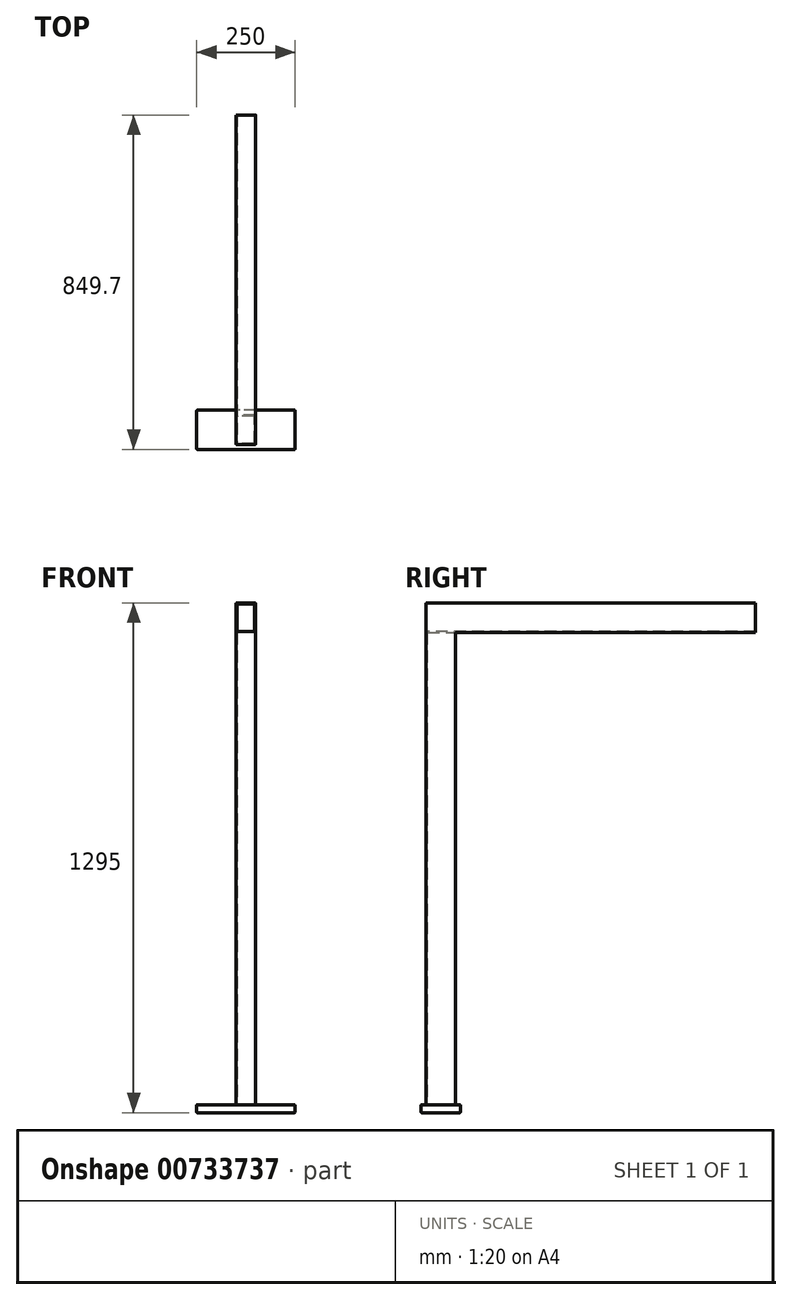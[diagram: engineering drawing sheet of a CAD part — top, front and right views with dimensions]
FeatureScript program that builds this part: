
annotation { "Feature Type Name" : "Feature", "Feature Type Description" : "" }
export const myFeature = defineFeature(function(context is Context, id is Id, definition is map)
    precondition{}
    {
        {
            var Q0;
            Q0=qCreatedBy(makeId("Top.planeOp"),FACE);
            var sketch = newSketch(context, id + "F0", { "sketchPlane" : qUnion([Q0])});
            skLineSegment(sketch, "E0.bottom", {"start": v(125, -50) * mm, "end": v(-125, -50) * mm});
            skLineSegment(sketch, "E0.top", {"start": v(125, 50) * mm, "end": v(-125, 50) * mm});
            skLineSegment(sketch, "E0.left", {"start": v(125, -50) * mm, "end": v(125, 50) * mm});
            skLineSegment(sketch, "E0.right", {"start": v(-125, -50) * mm, "end": v(-125, 50) * mm});
            skPoint(sketch, "E0.middle", {"position": v(0, 0) * mm});
            skSolve(sketch);
        }
        {
            var Q0;
            Q0=makeQuery(id+"F0.imprint","IMPRINT",FACE,{"disambiguationData":[TD([[makeQuery(id+"F0.imprint","IMPRINT",EDGE,{"derivedFrom":sQuery(id+"F0.wireOp",EDGE,"E0.bottom")}),-1.0]])]});
            extrude(context, id + "F1", {"entities" : qUnion([Q0]), "depth" : 20 * mm, "offsetDistance" : 25 * mm});
        }
        {
            var Q0;
            Q0=makeQuery(id+"F1.opExtrude","CAP_FACE",FACE,{"disambiguationData":[OSD([sQuery(id+"F0.wireOp",EDGE,"E0.bottom"),sQuery(id+"F0.wireOp",EDGE,"E0.top"),sQuery(id+"F0.wireOp",EDGE,"E0.left"),sQuery(id+"F0.wireOp",EDGE,"E0.right")])],"isStart":false});
            var sketch = newSketch(context, id + "F2", { "sketchPlane" : qUnion([Q0])});
            skLineSegment(sketch, "E1.bottom", {"start": v(25, -37.5) * mm, "end": v(-25, -37.5) * mm});
            skLineSegment(sketch, "E1.top", {"start": v(25, 37.5) * mm, "end": v(-25, 37.5) * mm});
            skLineSegment(sketch, "E1.left", {"start": v(25, -37.5) * mm, "end": v(25, 37.5) * mm});
            skLineSegment(sketch, "E1.right", {"start": v(-25, -37.5) * mm, "end": v(-25, 37.5) * mm});
            skPoint(sketch, "E1.middle", {"position": v(0, 0) * mm});
            skLineSegment(sketch, "E2.0", {"start": v(22, -34.5) * mm, "end": v(22, 34.5) * mm});
            skLineSegment(sketch, "E2.1", {"start": v(22, -34.5) * mm, "end": v(-22, -34.5) * mm});
            skLineSegment(sketch, "E2.2", {"start": v(-22, -34.5) * mm, "end": v(-22, 34.5) * mm});
            skLineSegment(sketch, "E2.3", {"start": v(22, 34.5) * mm, "end": v(-22, 34.5) * mm});
            skSolve(sketch);
        }
        {
            var Q0;
            Q0=makeQuery(id+"F2.imprint","IMPRINT",FACE,{"disambiguationData":[TD([[makeQuery(id+"F2.imprint","IMPRINT",EDGE,{"derivedFrom":sQuery(id+"F2.wireOp",EDGE,"E1.bottom")}),-1.0]])]});
            extrude(context, id + "F3", {"entities" : qUnion([Q0]), "operationType" : NewBodyOperationType.ADD, "depth" : 1200 * mm, "offsetDistance" : 25 * mm});
        }
        {
            var Q0;
            Q0=makeQuery(id+"F3.opExtrude","SWEPT_FACE",FACE,{"disambiguationData":[OSD([sQuery(id+"F2.wireOp",EDGE,"E1.bottom")])]});
            var sketch = newSketch(context, id + "F4", { "sketchPlane" : qUnion([Q0])});
            skLineSegment(sketch, "E3.bottom", {"start": v(25, 1220) * mm, "end": v(-25, 1220) * mm});
            skLineSegment(sketch, "E3.top", {"start": v(25, 1295) * mm, "end": v(-25, 1295) * mm});
            skLineSegment(sketch, "E3.left", {"start": v(25, 1220) * mm, "end": v(25, 1295) * mm});
            skLineSegment(sketch, "E3.right", {"start": v(-25, 1220) * mm, "end": v(-25, 1295) * mm});
            skLineSegment(sketch, "E4.0", {"start": v(-22, 1223) * mm, "end": v(-22, 1292) * mm});
            skLineSegment(sketch, "E4.1", {"start": v(22, 1223) * mm, "end": v(-22, 1223) * mm});
            skLineSegment(sketch, "E4.2", {"start": v(22, 1223) * mm, "end": v(22, 1292) * mm});
            skLineSegment(sketch, "E4.3", {"start": v(22, 1292) * mm, "end": v(-22, 1292) * mm});
            skSolve(sketch);
        }
        {
            var Q0;
            Q0=makeQuery(id+"F4.imprint","IMPRINT",FACE,{"disambiguationData":[TD([[makeQuery(id+"F4.imprint","IMPRINT",EDGE,{"derivedFrom":sQuery(id+"F4.wireOp",EDGE,"E3.bottom")}),-1.0]])]});
            extrude(context, id + "F5", {"entities" : qUnion([Q0]), "operationType" : NewBodyOperationType.ADD, "oppositeDirection" : true, "depth" : 837.2 * mm, "offsetDistance" : 25 * mm});
        }
        {
            var Q0;
            Q0=makeQuery(id+"F5.boolean.opBoolean","MERGE",EDGE,{"derivedFrom":[makeQuery(id+"F3.opExtrude","SWEPT_EDGE",EDGE,{"disambiguationData":[OSD([sQuery(id+"F2.wireOp",EDGE,"E1.bottom"),sQuery(id+"F2.wireOp",EDGE,"E1.right")])]}),makeQuery(id+"F5.opExtrude","CAP_EDGE",EDGE,{"disambiguationData":[OSD([sQuery(id+"F4.wireOp",EDGE,"E3.right")])],"isStart":true})]});
            var Q1;
            Q1=makeQuery(id+"F3.opExtrude","SWEPT_EDGE",EDGE,{"disambiguationData":[OSD([sQuery(id+"F2.wireOp",EDGE,"E1.top"),sQuery(id+"F2.wireOp",EDGE,"E1.left")])]});
            var Q2;
            Q2=makeQuery(id+"F5.boolean.opBoolean","MERGE",EDGE,{"derivedFrom":[makeQuery(id+"F3.opExtrude","SWEPT_EDGE",EDGE,{"disambiguationData":[OSD([sQuery(id+"F2.wireOp",EDGE,"E1.bottom"),sQuery(id+"F2.wireOp",EDGE,"E1.left")])]}),makeQuery(id+"F5.opExtrude","CAP_EDGE",EDGE,{"disambiguationData":[OSD([sQuery(id+"F4.wireOp",EDGE,"E3.left")])],"isStart":true})]});
            var Q3;
            Q3=makeQuery(id+"F3.opExtrude","SWEPT_EDGE",EDGE,{"disambiguationData":[OSD([sQuery(id+"F2.wireOp",EDGE,"E2.1"),sQuery(id+"F2.wireOp",EDGE,"E2.2")])]});
            var Q4;
            Q4=makeQuery(id+"F3.opExtrude","SWEPT_EDGE",EDGE,{"disambiguationData":[OSD([sQuery(id+"F2.wireOp",EDGE,"E2.0"),sQuery(id+"F2.wireOp",EDGE,"E2.3")])]});
            var Q5;
            Q5=makeQuery(id+"F3.opExtrude","SWEPT_EDGE",EDGE,{"disambiguationData":[OSD([sQuery(id+"F2.wireOp",EDGE,"E2.0"),sQuery(id+"F2.wireOp",EDGE,"E2.1")])]});
            var Q6;
            Q6=makeQuery(id+"F3.opExtrude","SWEPT_EDGE",EDGE,{"disambiguationData":[OSD([sQuery(id+"F2.wireOp",EDGE,"E2.2"),sQuery(id+"F2.wireOp",EDGE,"E2.3")])]});
            var Q7;
            Q7=makeQuery(id+"F3.opExtrude","SWEPT_EDGE",EDGE,{"disambiguationData":[OSD([sQuery(id+"F2.wireOp",EDGE,"E1.top"),sQuery(id+"F2.wireOp",EDGE,"E1.right")])]});
            var Q8;
            Q8=makeQuery(id+"F5.opExtrude","SWEPT_EDGE",EDGE,{"disambiguationData":[OSD([sQuery(id+"F4.wireOp",EDGE,"E3.top"),sQuery(id+"F4.wireOp",EDGE,"E3.left")])]});
            var Q9;
            Q9=makeQuery(id+"F5.opExtrude","SWEPT_EDGE",EDGE,{"disambiguationData":[OSD([sQuery(id+"F2.wireOp",EDGE,"E1.bottom"),sQuery(id+"F2.wireOp",EDGE,"E1.left"),sQuery(id+"F4.wireOp",EDGE,"E3.bottom"),sQuery(id+"F4.wireOp",EDGE,"E3.left")])]});
            var Q10;
            Q10=makeQuery(id+"F5.opExtrude","SWEPT_EDGE",EDGE,{"disambiguationData":[OSD([sQuery(id+"F4.wireOp",EDGE,"E3.top"),sQuery(id+"F4.wireOp",EDGE,"E3.right")])]});
            var Q11;
            Q11=makeQuery(id+"F5.opExtrude","SWEPT_EDGE",EDGE,{"disambiguationData":[OSD([sQuery(id+"F4.wireOp",EDGE,"E4.0"),sQuery(id+"F4.wireOp",EDGE,"E4.3")])]});
            var Q12;
            Q12=makeQuery(id+"F5.opExtrude","CAP_EDGE",EDGE,{"disambiguationData":[OSD([sQuery(id+"F4.wireOp",EDGE,"E4.0")])],"isStart":true});
            var Q13;
            Q13=makeQuery(id+"F5.opExtrude","CAP_EDGE",EDGE,{"disambiguationData":[OSD([sQuery(id+"F4.wireOp",EDGE,"E4.1")])],"isStart":true});
            var Q14;
            Q14=makeQuery(id+"F5.opExtrude","SWEPT_EDGE",EDGE,{"disambiguationData":[OSD([sQuery(id+"F4.wireOp",EDGE,"E4.2"),sQuery(id+"F4.wireOp",EDGE,"E4.3")])]});
            var Q15;
            Q15=makeQuery(id+"F3.opExtrude","CAP_EDGE",EDGE,{"disambiguationData":[OSD([sQuery(id+"F2.wireOp",EDGE,"E1.top")])],"isStart":false});
            var Q16;
            Q16=makeQuery(id+"F5.opExtrude","CAP_EDGE",EDGE,{"disambiguationData":[OSD([sQuery(id+"F4.wireOp",EDGE,"E3.top")])],"isStart":true});
            var Q17;
            Q17=makeQuery(id+"F5.opExtrude","SWEPT_EDGE",EDGE,{"disambiguationData":[OSD([sQuery(id+"F4.wireOp",EDGE,"E4.1"),sQuery(id+"F4.wireOp",EDGE,"E4.2")])]});
            var Q18;
            Q18=makeQuery(id+"F5.opExtrude","SWEPT_EDGE",EDGE,{"disambiguationData":[OSD([sQuery(id+"F4.wireOp",EDGE,"E4.0"),sQuery(id+"F4.wireOp",EDGE,"E4.1")])]});
            var Q19;
            Q19=makeQuery(id+"F3.opExtrude","CAP_EDGE",EDGE,{"disambiguationData":[OSD([sQuery(id+"F2.wireOp",EDGE,"E2.0")])],"isStart":false});
            var Q20;
            Q20=makeQuery(id+"F3.opExtrude","CAP_EDGE",EDGE,{"disambiguationData":[OSD([sQuery(id+"F2.wireOp",EDGE,"E2.1")])],"isStart":false});
            var Q21;
            Q21=makeQuery(id+"F3.opExtrude","CAP_EDGE",EDGE,{"disambiguationData":[OSD([sQuery(id+"F2.wireOp",EDGE,"E2.2")])],"isStart":false});
            var Q22;
            Q22=makeQuery(id+"F5.opExtrude","SWEPT_EDGE",EDGE,{"disambiguationData":[OSD([sQuery(id+"F2.wireOp",EDGE,"E1.bottom"),sQuery(id+"F2.wireOp",EDGE,"E1.right"),sQuery(id+"F4.wireOp",EDGE,"E3.bottom"),sQuery(id+"F4.wireOp",EDGE,"E3.right")])]});
            var Q23;
            Q23=makeQuery(id+"F3.opExtrude","CAP_EDGE",EDGE,{"disambiguationData":[OSD([sQuery(id+"F2.wireOp",EDGE,"E2.3")])],"isStart":false});
            var Q24;
            Q24=makeQuery(id+"F5.opExtrude","CAP_EDGE",EDGE,{"disambiguationData":[OSD([sQuery(id+"F4.wireOp",EDGE,"E4.3")])],"isStart":true});
            var Q25;
            Q25=makeQuery(id+"F5.opExtrude","CAP_EDGE",EDGE,{"disambiguationData":[OSD([sQuery(id+"F4.wireOp",EDGE,"E4.2")])],"isStart":true});
            var Q26;
            Q26=makeQuery(id+"F1.opExtrude","SWEPT_EDGE",EDGE,{"disambiguationData":[OSD([sQuery(id+"F0.wireOp",EDGE,"E0.bottom"),sQuery(id+"F0.wireOp",EDGE,"E0.left")])]});
            var Q27;
            Q27=makeQuery(id+"F1.opExtrude","SWEPT_EDGE",EDGE,{"disambiguationData":[OSD([sQuery(id+"F0.wireOp",EDGE,"E0.bottom"),sQuery(id+"F0.wireOp",EDGE,"E0.right")])]});
            var Q28;
            Q28=makeQuery(id+"F1.opExtrude","SWEPT_EDGE",EDGE,{"disambiguationData":[OSD([sQuery(id+"F0.wireOp",EDGE,"E0.top"),sQuery(id+"F0.wireOp",EDGE,"E0.left")])]});
            var Q29;
            Q29=makeQuery(id+"F1.opExtrude","CAP_EDGE",EDGE,{"disambiguationData":[OSD([sQuery(id+"F0.wireOp",EDGE,"E0.bottom")])],"isStart":true});
            var Q30;
            Q30=makeQuery(id+"F1.opExtrude","CAP_EDGE",EDGE,{"disambiguationData":[OSD([sQuery(id+"F0.wireOp",EDGE,"E0.bottom")])],"isStart":false});
            var Q31;
            Q31=makeQuery(id+"F1.opExtrude","CAP_EDGE",EDGE,{"disambiguationData":[OSD([sQuery(id+"F0.wireOp",EDGE,"E0.top")])],"isStart":false});
            var Q32;
            Q32=makeQuery(id+"F1.opExtrude","CAP_EDGE",EDGE,{"disambiguationData":[OSD([sQuery(id+"F0.wireOp",EDGE,"E0.left")])],"isStart":false});
            var Q33;
            Q33=makeQuery(id+"F1.opExtrude","CAP_EDGE",EDGE,{"disambiguationData":[OSD([sQuery(id+"F0.wireOp",EDGE,"E0.right")])],"isStart":false});
            var Q34;
            Q34=makeQuery(id+"F1.opExtrude","SWEPT_EDGE",EDGE,{"disambiguationData":[OSD([sQuery(id+"F0.wireOp",EDGE,"E0.top"),sQuery(id+"F0.wireOp",EDGE,"E0.right")])]});
            var Q35;
            Q35=makeQuery(id+"F1.opExtrude","CAP_EDGE",EDGE,{"disambiguationData":[OSD([sQuery(id+"F0.wireOp",EDGE,"E0.top")])],"isStart":true});
            var Q36;
            Q36=makeQuery(id+"F1.opExtrude","CAP_EDGE",EDGE,{"disambiguationData":[OSD([sQuery(id+"F0.wireOp",EDGE,"E0.left")])],"isStart":true});
            var Q37;
            Q37=makeQuery(id+"F1.opExtrude","CAP_EDGE",EDGE,{"disambiguationData":[OSD([sQuery(id+"F0.wireOp",EDGE,"E0.right")])],"isStart":true});
            var Q38;
            Q38=makeQuery(id+"F3.opExtrude","CAP_EDGE",EDGE,{"disambiguationData":[OSD([sQuery(id+"F2.wireOp",EDGE,"E1.bottom")])],"isStart":true});
            var Q39;
            Q39=makeQuery(id+"F3.opExtrude","CAP_EDGE",EDGE,{"disambiguationData":[OSD([sQuery(id+"F2.wireOp",EDGE,"E2.3")])],"isStart":true});
            var Q40;
            Q40=makeQuery(id+"F3.opExtrude","CAP_EDGE",EDGE,{"disambiguationData":[OSD([sQuery(id+"F2.wireOp",EDGE,"E2.2")])],"isStart":true});
            var Q41;
            Q41=makeQuery(id+"F3.opExtrude","CAP_EDGE",EDGE,{"disambiguationData":[OSD([sQuery(id+"F2.wireOp",EDGE,"E2.0")])],"isStart":true});
            var Q42;
            Q42=makeQuery(id+"F3.opExtrude","CAP_EDGE",EDGE,{"disambiguationData":[OSD([sQuery(id+"F2.wireOp",EDGE,"E1.right")])],"isStart":true});
            var Q43;
            Q43=makeQuery(id+"F3.opExtrude","CAP_EDGE",EDGE,{"disambiguationData":[OSD([sQuery(id+"F2.wireOp",EDGE,"E1.top")])],"isStart":true});
            var Q44;
            Q44=makeQuery(id+"F3.opExtrude","CAP_EDGE",EDGE,{"disambiguationData":[OSD([sQuery(id+"F2.wireOp",EDGE,"E2.1")])],"isStart":true});
            var Q45;
            Q45=makeQuery(id+"F3.opExtrude","CAP_EDGE",EDGE,{"disambiguationData":[OSD([sQuery(id+"F2.wireOp",EDGE,"E1.left")])],"isStart":true});
            fillet(context, id + "F6", {"entities" : qUnion([Q0, Q1, Q2, Q3, Q4, Q5, Q6, Q7, Q8, Q9, Q10, Q11, Q12, Q13, Q14, Q15, Q16, Q17, Q18, Q19, Q20, Q21, Q22, Q23, Q24, Q25, Q26, Q27, Q28, Q29, Q30, Q31, Q32, Q33, Q34, Q35, Q36, Q37, Q38, Q39, Q40, Q41, Q42, Q43, Q44, Q45]), "radius" : 1.5 * mm, "tangentPropagation" : true, "allowEdgeOverflow" : false});
        }
    });
